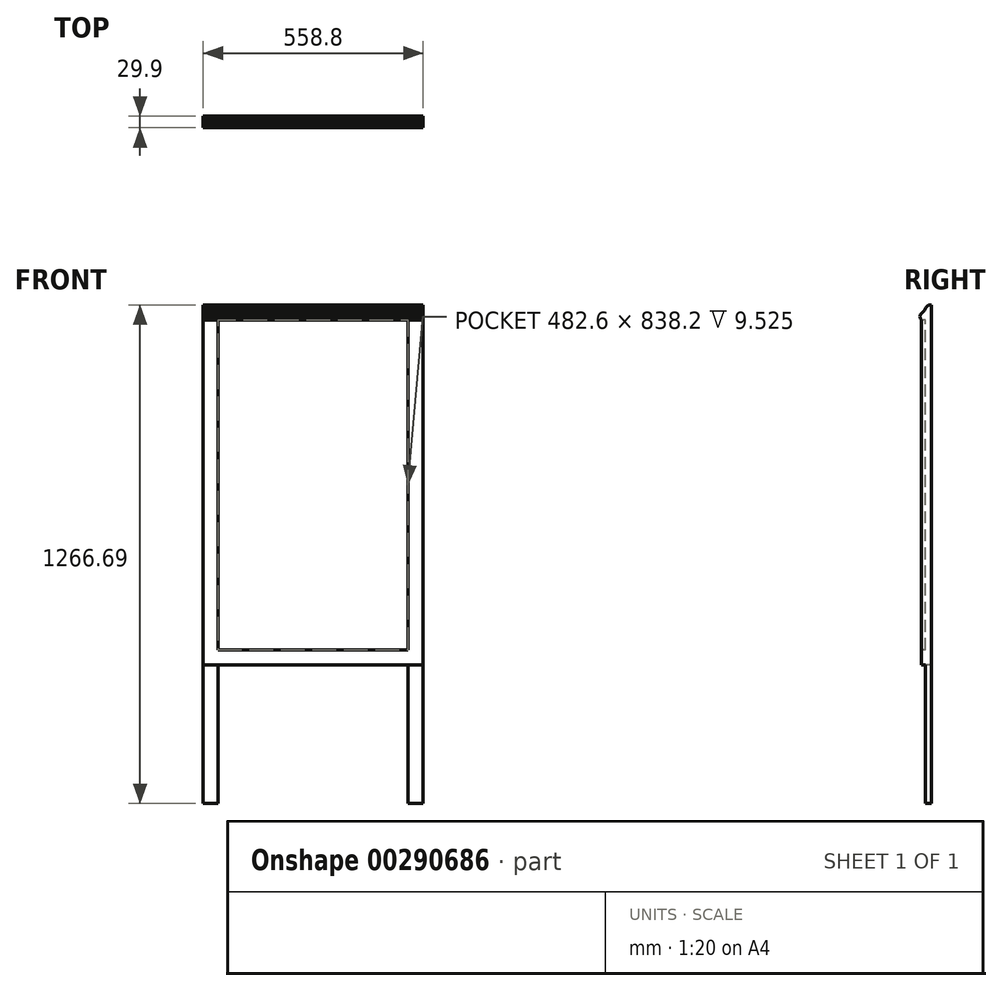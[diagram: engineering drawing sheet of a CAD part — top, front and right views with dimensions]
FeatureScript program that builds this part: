
annotation { "Feature Type Name" : "Feature", "Feature Type Description" : "" }
export const myFeature = defineFeature(function(context is Context, id is Id, definition is map)
    precondition{}
    {
        {
            var Q0;
            Q0=qCreatedBy(makeId("Front.planeOp"),FACE);
            var sketch = newSketch(context, id + "F0", { "sketchPlane" : qUnion([Q0])});
            skLineSegment(sketch, "E0.bottom", {"start": v(0, 0) * mm, "end": v(558.8, 0) * mm});
            skLineSegment(sketch, "E0.top", {"start": v(0, 914.4) * mm, "end": v(558.8, 914.4) * mm});
            skLineSegment(sketch, "E0.left", {"start": v(0, 0) * mm, "end": v(0, 914.4) * mm});
            skLineSegment(sketch, "E0.right", {"start": v(558.8, 0) * mm, "end": v(558.8, 914.4) * mm});
            skSolve(sketch);
        }
        {
            var Q0;
            Q0 = qSketchRegion(id + "F0", true);
            extrude(context, id + "F1", {"entities" : qUnion([Q0]), "depth" : 25.4 * mm});
        }
        {
            var Q0;
            Q0=makeQuery(id+"F1.opExtrude","CAP_FACE",FACE,{"disambiguationData":[OSD([sQuery(id+"F0.wireOp",EDGE,"E0.bottom"),sQuery(id+"F0.wireOp",EDGE,"E0.top"),sQuery(id+"F0.wireOp",EDGE,"E0.left"),sQuery(id+"F0.wireOp",EDGE,"E0.right")])],"isStart":false});
            var sketch = newSketch(context, id + "F2", { "sketchPlane" : qUnion([Q0])});
            skLineSegment(sketch, "E1.0", {"start": v(520.7, 876.3) * mm, "end": v(38.1, 876.3) * mm});
            skLineSegment(sketch, "E1.1", {"start": v(520.7, 38.1) * mm, "end": v(520.7, 876.3) * mm});
            skLineSegment(sketch, "E1.2", {"start": v(38.1, 38.1) * mm, "end": v(520.7, 38.1) * mm});
            skLineSegment(sketch, "E1.3", {"start": v(38.1, 876.3) * mm, "end": v(38.1, 38.1) * mm});
            skSolve(sketch);
        }
        {
            var Q0;
            Q0 = qSketchRegion(id + "F2", true);
            extrude(context, id + "F3", {"entities" : qUnion([Q0]), "operationType" : NewBodyOperationType.REMOVE, "oppositeDirection" : true, "depth" : 9.52 * mm});
        }
        {
            var Q0;
            Q0=makeQuery(id+"F3.boolean.opBoolean","COPY",FACE,{"derivedFrom":makeQuery(id+"F3.opExtrude","CAP_FACE",FACE,{"disambiguationData":[OSD([sQuery(id+"F2.wireOp",EDGE,"E1.0"),sQuery(id+"F2.wireOp",EDGE,"E1.1"),sQuery(id+"F2.wireOp",EDGE,"E1.2"),sQuery(id+"F2.wireOp",EDGE,"E1.3")])],"isStart":false})});
            var sketch = newSketch(context, id + "F4", { "sketchPlane" : qUnion([Q0])});
            skLineSegment(sketch, "E2.bottom", {"start": v(38.1, 38.1) * mm, "end": v(0, 38.1) * mm});
            skLineSegment(sketch, "E2.top", {"start": v(38.1, -352.3) * mm, "end": v(0, -352.3) * mm});
            skLineSegment(sketch, "E2.left", {"start": v(38.1, 38.1) * mm, "end": v(38.1, -352.3) * mm});
            skLineSegment(sketch, "E2.right", {"start": v(0, 38.1) * mm, "end": v(0, -352.3) * mm});
            skLineSegment(sketch, "E3.bottom", {"start": v(520.7, 38.1) * mm, "end": v(558.8, 38.1) * mm});
            skLineSegment(sketch, "E3.top", {"start": v(520.7, -352.3) * mm, "end": v(558.8, -352.3) * mm});
            skLineSegment(sketch, "E3.left", {"start": v(520.7, 38.1) * mm, "end": v(520.7, -352.3) * mm});
            skLineSegment(sketch, "E3.right", {"start": v(558.8, 38.1) * mm, "end": v(558.8, -352.3) * mm});
            skSolve(sketch);
        }
        {
            var Q0;
            Q0 = qSketchRegion(id + "F4", true);
            var Q1;
            Q1=makeQuery(id+"F1.opExtrude","CAP_FACE",FACE,{"disambiguationData":[OSD([sQuery(id+"F0.wireOp",EDGE,"E0.bottom"),sQuery(id+"F0.wireOp",EDGE,"E0.top"),sQuery(id+"F0.wireOp",EDGE,"E0.left"),sQuery(id+"F0.wireOp",EDGE,"E0.right")])],"isStart":true});
            extrude(context, id + "F5", {"entities" : qUnion([Q0]), "operationType" : NewBodyOperationType.ADD, "endBound" : BoundingType.UP_TO_SURFACE, "oppositeDirection" : true, "endBoundEntityFace" : qUnion([Q1]), "depth" : 25.4 * mm});
        }
        {
            var Q0;
            Q0=makeQuery(id+"F5.boolean.opBoolean","MERGE",FACE,{"derivedFrom":[makeQuery(id+"F1.opExtrude","SWEPT_FACE",FACE,{"disambiguationData":[OSD([sQuery(id+"F0.wireOp",EDGE,"E0.right")])]}),makeQuery(id+"F5.opExtrude","SWEPT_FACE",FACE,{"disambiguationData":[OSD([sQuery(id+"F4.wireOp",EDGE,"E3.right")])]})]});
            var sketch = newSketch(context, id + "F6", { "sketchPlane" : qUnion([Q0])});
            skLineSegment(sketch, "E4", {"start": v(-8.41, 914.4) * mm, "end": v(-14.5, 908.1) * mm});
            skLineSegment(sketch, "E5", {"start": v(-14.5, 908.1) * mm, "end": v(-17.4, 899.98) * mm});
            skLineSegment(sketch, "E6", {"start": v(-17.4, 899.98) * mm, "end": v(-25.4, 892.73) * mm});
            skSolve(sketch);
        }
        {
            var Q0;
            {var subQ4=sQuery(id+"F6.wireOp",EDGE,"E4");Q0=makeQuery(id+"F6.imprint","IMPRINT",FACE,{"disambiguationData":[TD([[makeQuery(id+"F6.imprint","IMPRINT",EDGE,{"derivedFrom":subQ4}),-1.0]])]});}
            var Q1;
            Q1 = qSketchRegion(id + "F6", true);
            extrude(context, id + "F7", {"entities" : qUnion([Q0, Q1]), "operationType" : NewBodyOperationType.REMOVE, "endBound" : BoundingType.THROUGH_ALL, "oppositeDirection" : true, "depth" : 25.4 * mm});
        }
        {
            var Q0;
            Q0=makeQuery(id+"F5.boolean.opBoolean","MERGE",FACE,{"derivedFrom":[makeQuery(id+"F1.opExtrude","SWEPT_FACE",FACE,{"disambiguationData":[OSD([sQuery(id+"F0.wireOp",EDGE,"E0.right")])]}),makeQuery(id+"F5.opExtrude","SWEPT_FACE",FACE,{"disambiguationData":[OSD([sQuery(id+"F4.wireOp",EDGE,"E3.right")])]})]});
            var sketch = newSketch(context, id + "F8", { "sketchPlane" : qUnion([Q0])});
            skLineSegment(sketch, "E7", {"start": v(-25.4, 892.73) * mm, "end": v(-28.54, 889.69) * mm});
            skLineSegment(sketch, "E8", {"start": v(-28.54, 889.69) * mm, "end": v(-29.9, 884.58) * mm});
            skLineSegment(sketch, "E9", {"start": v(-29.9, 884.58) * mm, "end": v(-28.54, 880.16) * mm});
            skLineSegment(sketch, "E10", {"start": v(-28.54, 880.16) * mm, "end": v(-25.4, 876.3) * mm});
            skSolve(sketch);
        }
        {
            var Q0;
            {var subQ1=sQuery(id+"F8.wireOp",EDGE,"E7");Q0=makeQuery(id+"F8.imprint","IMPRINT",FACE,{"disambiguationData":[TD([[makeQuery(id+"F8.imprint","IMPRINT",EDGE,{"derivedFrom":subQ1}),1.0]])]});}
            var Q1;
            Q1 = qSketchRegion(id + "F8", true);
            var Q2;
            Q2=makeQuery(id+"F5.boolean.opBoolean","MERGE",FACE,{"derivedFrom":[makeQuery(id+"F1.opExtrude","SWEPT_FACE",FACE,{"disambiguationData":[OSD([sQuery(id+"F0.wireOp",EDGE,"E0.left")])]}),makeQuery(id+"F5.opExtrude","SWEPT_FACE",FACE,{"disambiguationData":[OSD([sQuery(id+"F4.wireOp",EDGE,"E2.right")])]})]});
            extrude(context, id + "F9", {"entities" : qUnion([Q0, Q1]), "operationType" : NewBodyOperationType.ADD, "endBound" : BoundingType.UP_TO_SURFACE, "oppositeDirection" : true, "endBoundEntityFace" : qUnion([Q2]), "depth" : 25.4 * mm});
        }
    });
